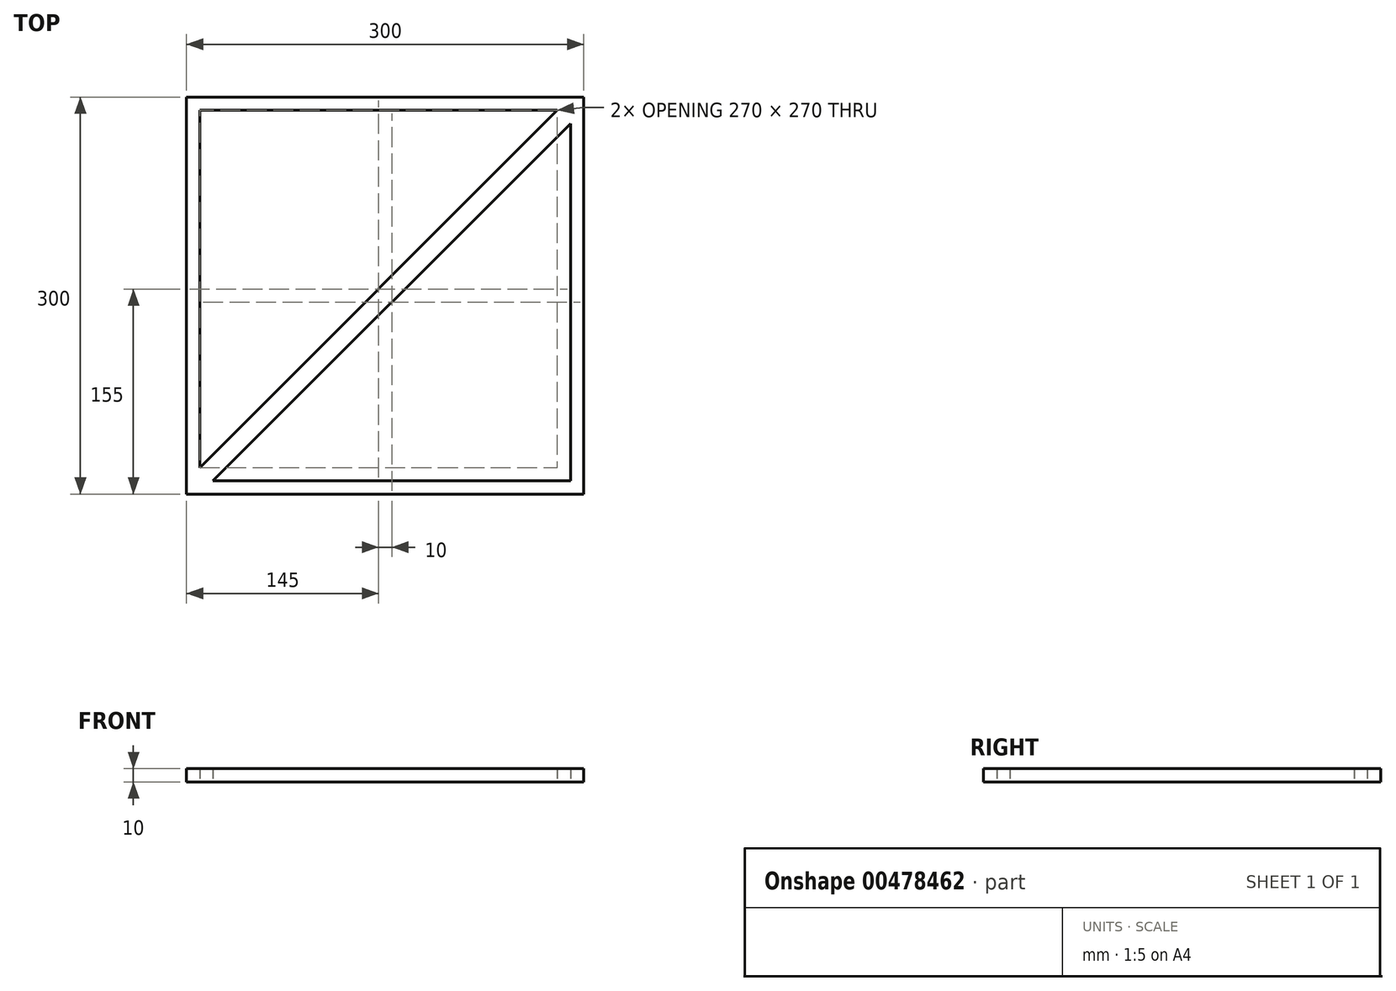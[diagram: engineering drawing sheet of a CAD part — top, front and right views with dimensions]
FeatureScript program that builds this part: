
annotation { "Feature Type Name" : "Feature", "Feature Type Description" : "" }
export const myFeature = defineFeature(function(context is Context, id is Id, definition is map)
    precondition{}
    {
        {
            var Q0;
            Q0=qCreatedBy(makeId("Top.planeOp"),FACE);
            var sketch = newSketch(context, id + "F0", { "sketchPlane" : qUnion([Q0])});
            skLineSegment(sketch, "E0.bottom", {"start": v(0, 0) * mm, "end": v(300, 0) * mm});
            skLineSegment(sketch, "E0.top", {"start": v(0, 300) * mm, "end": v(300, 300) * mm});
            skLineSegment(sketch, "E0.left", {"start": v(0, 0) * mm, "end": v(0, 300) * mm});
            skLineSegment(sketch, "E0.right", {"start": v(300, 0) * mm, "end": v(300, 300) * mm});
            skLineSegment(sketch, "E1", {"start": v(280, 290) * mm, "end": v(10, 290) * mm});
            skLineSegment(sketch, "E2", {"start": v(10, 290) * mm, "end": v(10, 20) * mm});
            skLineSegment(sketch, "E3", {"start": v(10, 20) * mm, "end": v(280, 290) * mm});
            skLineSegment(sketch, "E4", {"start": v(290, 280) * mm, "end": v(290, 10) * mm});
            skLineSegment(sketch, "E5", {"start": v(290, 10) * mm, "end": v(20, 10) * mm});
            skLineSegment(sketch, "E6", {"start": v(290, 280) * mm, "end": v(20, 10) * mm});
            skSolve(sketch);
        }
        {
            var Q0;
            Q0=makeQuery(id+"F0.imprint","IMPRINT",FACE,{"disambiguationData":[TD([[makeQuery(id+"F0.imprint","IMPRINT",EDGE,{"derivedFrom":sQuery(id+"F0.wireOp",EDGE,"E0.bottom")}),1.0]])]});
            extrude(context, id + "F1", {"entities" : qUnion([Q0]), "depth" : 10 * mm});
        }
    });
